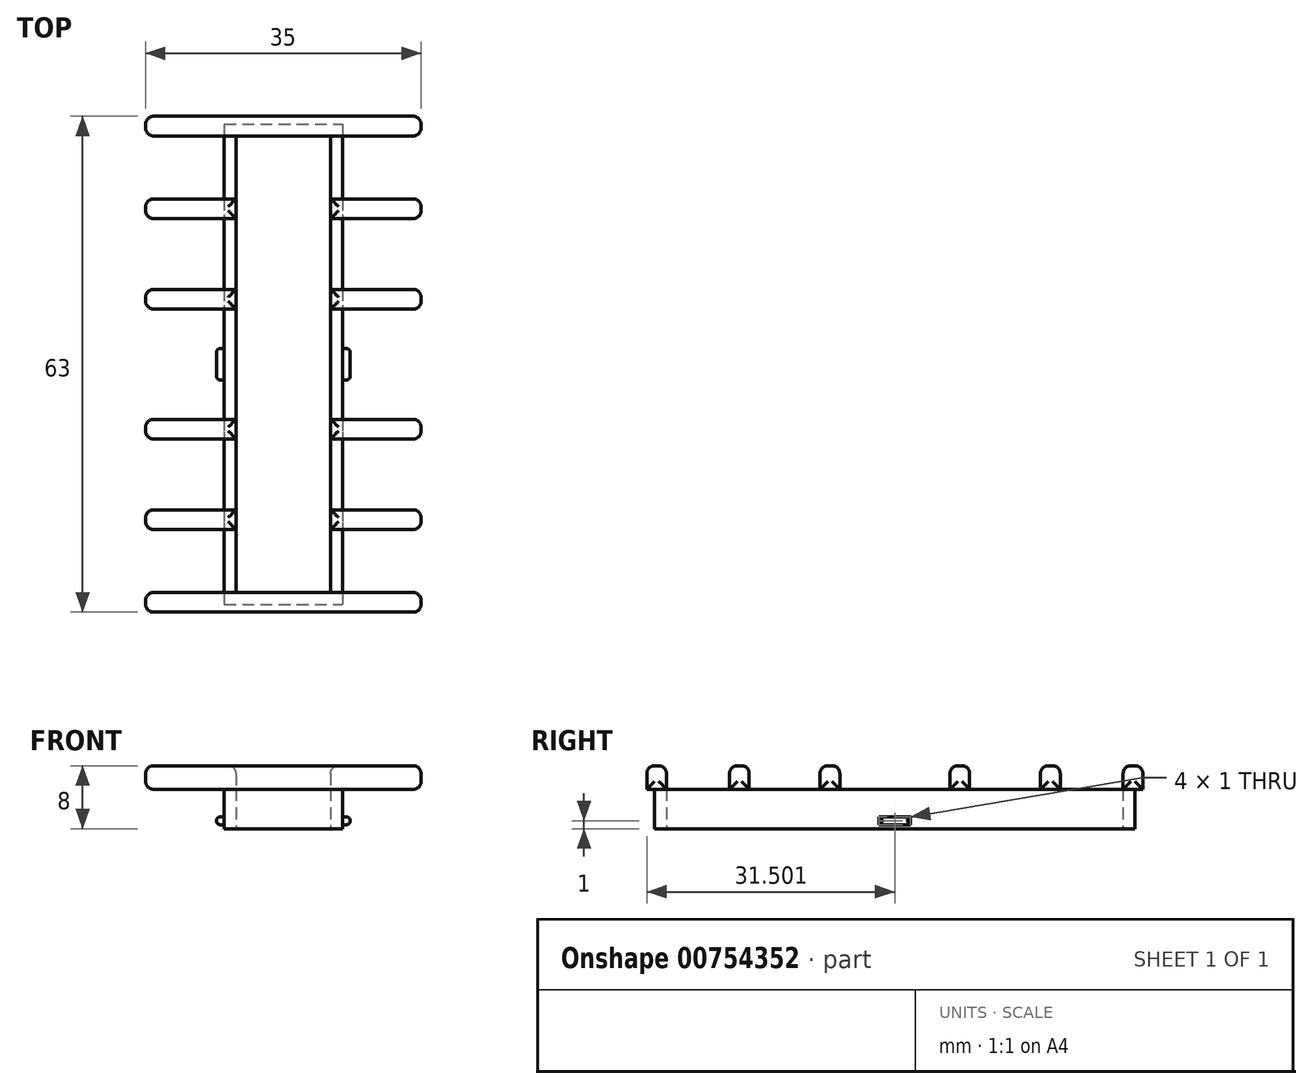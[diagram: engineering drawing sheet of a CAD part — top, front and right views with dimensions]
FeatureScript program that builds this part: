
annotation { "Feature Type Name" : "Feature", "Feature Type Description" : "" }
export const myFeature = defineFeature(function(context is Context, id is Id, definition is map)
    precondition{}
    {
        {
            var Q0;
            Q0=qCreatedBy(makeId("Top.planeOp"),FACE);
            var sketch = newSketch(context, id + "F0", { "sketchPlane" : qUnion([Q0])});
            skLineSegment(sketch, "E0.bottom", {"start": v(-47.35, 57.33) * mm, "end": v(-32.35, 57.33) * mm});
            skLineSegment(sketch, "E0.top", {"start": v(-47.35, -3.67) * mm, "end": v(-32.35, -3.67) * mm});
            skLineSegment(sketch, "E0.left", {"start": v(-47.35, 57.33) * mm, "end": v(-47.35, -3.67) * mm});
            skLineSegment(sketch, "E0.right", {"start": v(-32.35, 57.33) * mm, "end": v(-32.35, -3.67) * mm});
            skLineSegment(sketch, "E1.0", {"start": v(-45.85, 55.83) * mm, "end": v(-33.85, 55.83) * mm});
            skLineSegment(sketch, "E1.1", {"start": v(-45.85, 55.83) * mm, "end": v(-45.85, -2.17) * mm});
            skLineSegment(sketch, "E1.2", {"start": v(-45.85, -2.17) * mm, "end": v(-33.85, -2.17) * mm});
            skLineSegment(sketch, "E1.3", {"start": v(-33.85, 55.83) * mm, "end": v(-33.85, -2.17) * mm});
            skSolve(sketch);
        }
        {
            var Q0;
            Q0 = qSketchRegion(id + "F0", true);
            extrude(context, id + "F1", {"entities" : qUnion([Q0]), "depth" : 5 * mm, "offsetDistance" : 25 * mm});
        }
        {
            var Q0;
            Q0=makeQuery(id+"F1.opExtrude","CAP_FACE",FACE,{"disambiguationData":[OSD([sQuery(id+"F0.wireOp",EDGE,"E0.bottom"),sQuery(id+"F0.wireOp",EDGE,"E0.top"),sQuery(id+"F0.wireOp",EDGE,"E0.left"),sQuery(id+"F0.wireOp",EDGE,"E0.right"),sQuery(id+"F0.wireOp",EDGE,"E1.0"),sQuery(id+"F0.wireOp",EDGE,"E1.1"),sQuery(id+"F0.wireOp",EDGE,"E1.2"),sQuery(id+"F0.wireOp",EDGE,"E1.3")])],"isStart":false});
            var sketch = newSketch(context, id + "F2", { "sketchPlane" : qUnion([Q0])});
            skLineSegment(sketch, "E2.bottom", {"start": v(-39.85, 55.83) * mm, "end": v(-22.35, 55.83) * mm});
            skLineSegment(sketch, "E2.top", {"start": v(-39.85, 58.33) * mm, "end": v(-22.35, 58.33) * mm});
            skLineSegment(sketch, "E2.left", {"start": v(-39.85, 55.83) * mm, "end": v(-39.85, 58.33) * mm});
            skLineSegment(sketch, "E2.right", {"start": v(-22.35, 55.83) * mm, "end": v(-22.35, 58.33) * mm});
            skLineSegment(sketch, "E3.MirrorCS", {"start": v(-39.85, 58.33) * mm, "end": v(-57.35, 58.33) * mm});
            skLineSegment(sketch, "E4.MirrorCS", {"start": v(-39.85, 55.83) * mm, "end": v(-57.35, 55.83) * mm});
            skLineSegment(sketch, "E5.MirrorCS", {"start": v(-57.35, 55.83) * mm, "end": v(-57.35, 58.33) * mm});
            skLineSegment(sketch, "E6.bottom", {"start": v(-39.85, -2.17) * mm, "end": v(-22.35, -2.17) * mm});
            skLineSegment(sketch, "E6.top", {"start": v(-39.85, -4.67) * mm, "end": v(-22.35, -4.67) * mm});
            skLineSegment(sketch, "E6.left", {"start": v(-39.85, -2.17) * mm, "end": v(-39.85, -4.67) * mm});
            skLineSegment(sketch, "E6.right", {"start": v(-22.35, -2.17) * mm, "end": v(-22.35, -4.67) * mm});
            skLineSegment(sketch, "E7.MirrorCS", {"start": v(-39.85, -2.17) * mm, "end": v(-57.35, -2.17) * mm});
            skLineSegment(sketch, "E8.MirrorCS", {"start": v(-57.35, -2.17) * mm, "end": v(-57.35, -4.67) * mm});
            skLineSegment(sketch, "E9.MirrorCS", {"start": v(-39.85, -4.67) * mm, "end": v(-57.35, -4.67) * mm});
            skLineSegment(sketch, "E10.bottom", {"start": v(-33.85, 36.33) * mm, "end": v(-22.35, 36.33) * mm});
            skLineSegment(sketch, "E10.top", {"start": v(-33.85, 33.83) * mm, "end": v(-22.35, 33.83) * mm});
            skLineSegment(sketch, "E10.left", {"start": v(-33.85, 36.33) * mm, "end": v(-33.85, 33.83) * mm});
            skLineSegment(sketch, "E10.right", {"start": v(-22.35, 36.33) * mm, "end": v(-22.35, 33.83) * mm});
            skLineSegment(sketch, "E11.bottom", {"start": v(-33.85, 19.83) * mm, "end": v(-22.35, 19.83) * mm});
            skLineSegment(sketch, "E11.top", {"start": v(-33.85, 17.33) * mm, "end": v(-22.35, 17.33) * mm});
            skLineSegment(sketch, "E11.left", {"start": v(-33.85, 19.83) * mm, "end": v(-33.85, 17.33) * mm});
            skLineSegment(sketch, "E11.right", {"start": v(-22.35, 19.83) * mm, "end": v(-22.35, 17.33) * mm});
            skLineSegment(sketch, "E12.bottom", {"start": v(-45.85, 17.33) * mm, "end": v(-57.35, 17.33) * mm});
            skLineSegment(sketch, "E12.top", {"start": v(-45.85, 19.83) * mm, "end": v(-57.35, 19.83) * mm});
            skLineSegment(sketch, "E12.left", {"start": v(-45.85, 17.33) * mm, "end": v(-45.85, 19.83) * mm});
            skLineSegment(sketch, "E12.right", {"start": v(-57.35, 17.33) * mm, "end": v(-57.35, 19.83) * mm});
            skLineSegment(sketch, "E13.bottom", {"start": v(-45.85, 33.83) * mm, "end": v(-57.35, 33.83) * mm});
            skLineSegment(sketch, "E13.top", {"start": v(-45.85, 36.33) * mm, "end": v(-57.35, 36.33) * mm});
            skLineSegment(sketch, "E13.left", {"start": v(-45.85, 33.83) * mm, "end": v(-45.85, 36.33) * mm});
            skLineSegment(sketch, "E13.right", {"start": v(-57.35, 33.83) * mm, "end": v(-57.35, 36.33) * mm});
            skLineSegment(sketch, "E14.bottom", {"start": v(-33.85, 47.83) * mm, "end": v(-22.35, 47.83) * mm});
            skLineSegment(sketch, "E14.top", {"start": v(-33.85, 45.33) * mm, "end": v(-22.35, 45.33) * mm});
            skLineSegment(sketch, "E14.left", {"start": v(-33.85, 47.83) * mm, "end": v(-33.85, 45.33) * mm});
            skLineSegment(sketch, "E14.right", {"start": v(-22.35, 47.83) * mm, "end": v(-22.35, 45.33) * mm});
            skLineSegment(sketch, "E15.bottom", {"start": v(-33.85, 8.33) * mm, "end": v(-22.35, 8.33) * mm});
            skLineSegment(sketch, "E15.top", {"start": v(-33.85, 5.83) * mm, "end": v(-22.35, 5.83) * mm});
            skLineSegment(sketch, "E15.left", {"start": v(-33.85, 8.33) * mm, "end": v(-33.85, 5.83) * mm});
            skLineSegment(sketch, "E15.right", {"start": v(-22.35, 8.33) * mm, "end": v(-22.35, 5.83) * mm});
            skLineSegment(sketch, "E16.bottom", {"start": v(-45.85, 45.33) * mm, "end": v(-57.35, 45.33) * mm});
            skLineSegment(sketch, "E16.top", {"start": v(-45.85, 47.83) * mm, "end": v(-57.35, 47.83) * mm});
            skLineSegment(sketch, "E16.left", {"start": v(-45.85, 45.33) * mm, "end": v(-45.85, 47.83) * mm});
            skLineSegment(sketch, "E16.right", {"start": v(-57.35, 45.33) * mm, "end": v(-57.35, 47.83) * mm});
            skLineSegment(sketch, "E17.bottom", {"start": v(-45.85, 5.83) * mm, "end": v(-57.35, 5.83) * mm});
            skLineSegment(sketch, "E17.top", {"start": v(-45.85, 8.33) * mm, "end": v(-57.35, 8.33) * mm});
            skLineSegment(sketch, "E17.left", {"start": v(-45.85, 5.83) * mm, "end": v(-45.85, 8.33) * mm});
            skLineSegment(sketch, "E17.right", {"start": v(-57.35, 5.83) * mm, "end": v(-57.35, 8.33) * mm});
            skSolve(sketch);
        }
        {
            var Q0;
            Q0 = qSketchRegion(id + "F2", true);
            extrude(context, id + "F3", {"entities" : qUnion([Q0]), "operationType" : NewBodyOperationType.ADD, "depth" : 3 * mm, "offsetDistance" : 25 * mm});
        }
        {
            var Q0;
            Q0=makeQuery(id+"F3.opExtrude","SWEPT_FACE",FACE,{"disambiguationData":[OSD([sQuery(id+"F2.wireOp",EDGE,"E2.right")])]});
            var Q1;
            Q1=makeQuery(id+"F3.opExtrude","SWEPT_FACE",FACE,{"disambiguationData":[OSD([sQuery(id+"F2.wireOp",EDGE,"E14.right")])]});
            var Q2;
            Q2=makeQuery(id+"F3.opExtrude","SWEPT_FACE",FACE,{"disambiguationData":[OSD([sQuery(id+"F2.wireOp",EDGE,"E10.right")])]});
            var Q3;
            Q3=makeQuery(id+"F3.opExtrude","SWEPT_FACE",FACE,{"disambiguationData":[OSD([sQuery(id+"F2.wireOp",EDGE,"E11.right")])]});
            var Q4;
            Q4=makeQuery(id+"F3.opExtrude","SWEPT_FACE",FACE,{"disambiguationData":[OSD([sQuery(id+"F2.wireOp",EDGE,"E15.right")])]});
            var Q5;
            Q5=makeQuery(id+"F3.opExtrude","SWEPT_FACE",FACE,{"disambiguationData":[OSD([sQuery(id+"F2.wireOp",EDGE,"E6.right")])]});
            var Q6;
            Q6=makeQuery(id+"F3.opExtrude","CAP_EDGE",EDGE,{"disambiguationData":[OSD([sQuery(id+"F2.wireOp",EDGE,"E16.left")])],"isStart":false});
            var Q7;
            Q7=makeQuery(id+"F3.opExtrude","CAP_EDGE",EDGE,{"disambiguationData":[OSD([sQuery(id+"F2.wireOp",EDGE,"E13.left")])],"isStart":false});
            var Q8;
            Q8=makeQuery(id+"F3.opExtrude","CAP_EDGE",EDGE,{"disambiguationData":[OSD([sQuery(id+"F2.wireOp",EDGE,"E12.left")])],"isStart":false});
            var Q9;
            Q9=makeQuery(id+"F3.opExtrude","CAP_EDGE",EDGE,{"disambiguationData":[OSD([sQuery(id+"F2.wireOp",EDGE,"E17.left")])],"isStart":false});
            var Q10;
            Q10=makeQuery(id+"F3.opExtrude","SWEPT_FACE",FACE,{"disambiguationData":[OSD([sQuery(id+"F2.wireOp",EDGE,"E8.MirrorCS")])]});
            var Q11;
            Q11=makeQuery(id+"F3.opExtrude","SWEPT_FACE",FACE,{"disambiguationData":[OSD([sQuery(id+"F2.wireOp",EDGE,"E17.right")])]});
            var Q12;
            Q12=makeQuery(id+"F3.opExtrude","SWEPT_FACE",FACE,{"disambiguationData":[OSD([sQuery(id+"F2.wireOp",EDGE,"E12.right")])]});
            var Q13;
            Q13=makeQuery(id+"F3.opExtrude","SWEPT_FACE",FACE,{"disambiguationData":[OSD([sQuery(id+"F2.wireOp",EDGE,"E13.right")])]});
            var Q14;
            Q14=makeQuery(id+"F3.opExtrude","SWEPT_FACE",FACE,{"disambiguationData":[OSD([sQuery(id+"F2.wireOp",EDGE,"E16.right")])]});
            var Q15;
            Q15=makeQuery(id+"F3.opExtrude","SWEPT_FACE",FACE,{"disambiguationData":[OSD([sQuery(id+"F2.wireOp",EDGE,"E5.MirrorCS")])]});
            var Q16;
            Q16=makeQuery(id+"F3.opExtrude","CAP_EDGE",EDGE,{"disambiguationData":[OSD([sQuery(id+"F2.wireOp",EDGE,"E14.left")])],"isStart":false});
            var Q17;
            Q17=makeQuery(id+"F3.opExtrude","CAP_EDGE",EDGE,{"disambiguationData":[OSD([sQuery(id+"F2.wireOp",EDGE,"E10.left")])],"isStart":false});
            var Q18;
            Q18=makeQuery(id+"F3.opExtrude","CAP_EDGE",EDGE,{"disambiguationData":[OSD([sQuery(id+"F2.wireOp",EDGE,"E11.left")])],"isStart":false});
            var Q19;
            Q19=makeQuery(id+"F3.opExtrude","CAP_EDGE",EDGE,{"disambiguationData":[OSD([sQuery(id+"F2.wireOp",EDGE,"E15.left")])],"isStart":false});
            var Q20;
            Q20=makeQuery(id+"F3.opExtrude","CAP_EDGE",EDGE,{"disambiguationData":[OSD([sQuery(id+"F2.wireOp",EDGE,"E2.bottom"),sQuery(id+"F2.wireOp",EDGE,"E4.MirrorCS")])],"isStart":false});
            var Q21;
            Q21=makeQuery(id+"F3.opExtrude","CAP_EDGE",EDGE,{"disambiguationData":[OSD([sQuery(id+"F2.wireOp",EDGE,"E16.bottom")])],"isStart":false});
            var Q22;
            Q22=makeQuery(id+"F3.opExtrude","CAP_EDGE",EDGE,{"disambiguationData":[OSD([sQuery(id+"F2.wireOp",EDGE,"E14.top")])],"isStart":false});
            var Q23;
            Q23=makeQuery(id+"F3.opExtrude","CAP_EDGE",EDGE,{"disambiguationData":[OSD([sQuery(id+"F2.wireOp",EDGE,"E13.bottom")])],"isStart":false});
            var Q24;
            Q24=makeQuery(id+"F3.opExtrude","CAP_EDGE",EDGE,{"disambiguationData":[OSD([sQuery(id+"F2.wireOp",EDGE,"E10.top")])],"isStart":false});
            var Q25;
            Q25=makeQuery(id+"F3.opExtrude","CAP_EDGE",EDGE,{"disambiguationData":[OSD([sQuery(id+"F2.wireOp",EDGE,"E12.bottom")])],"isStart":false});
            var Q26;
            Q26=makeQuery(id+"F3.opExtrude","CAP_EDGE",EDGE,{"disambiguationData":[OSD([sQuery(id+"F2.wireOp",EDGE,"E11.top")])],"isStart":false});
            var Q27;
            Q27=makeQuery(id+"F3.opExtrude","CAP_EDGE",EDGE,{"disambiguationData":[OSD([sQuery(id+"F2.wireOp",EDGE,"E17.bottom")])],"isStart":false});
            var Q28;
            Q28=makeQuery(id+"F3.opExtrude","CAP_EDGE",EDGE,{"disambiguationData":[OSD([sQuery(id+"F2.wireOp",EDGE,"E15.top")])],"isStart":false});
            var Q29;
            Q29=makeQuery(id+"F3.opExtrude","CAP_EDGE",EDGE,{"disambiguationData":[OSD([sQuery(id+"F2.wireOp",EDGE,"E6.top"),sQuery(id+"F2.wireOp",EDGE,"E9.MirrorCS")])],"isStart":false});
            var Q30;
            Q30=makeQuery(id+"F3.opExtrude","CAP_EDGE",EDGE,{"disambiguationData":[OSD([sQuery(id+"F2.wireOp",EDGE,"E6.bottom"),sQuery(id+"F2.wireOp",EDGE,"E7.MirrorCS")])],"isStart":false});
            var Q31;
            Q31=makeQuery(id+"F3.opExtrude","CAP_EDGE",EDGE,{"disambiguationData":[OSD([sQuery(id+"F2.wireOp",EDGE,"E17.top")])],"isStart":false});
            var Q32;
            Q32=makeQuery(id+"F3.opExtrude","CAP_EDGE",EDGE,{"disambiguationData":[OSD([sQuery(id+"F2.wireOp",EDGE,"E15.bottom")])],"isStart":false});
            var Q33;
            Q33=makeQuery(id+"F3.opExtrude","CAP_EDGE",EDGE,{"disambiguationData":[OSD([sQuery(id+"F2.wireOp",EDGE,"E11.bottom")])],"isStart":false});
            var Q34;
            Q34=makeQuery(id+"F3.opExtrude","CAP_EDGE",EDGE,{"disambiguationData":[OSD([sQuery(id+"F2.wireOp",EDGE,"E12.top")])],"isStart":false});
            var Q35;
            Q35=makeQuery(id+"F3.opExtrude","CAP_EDGE",EDGE,{"disambiguationData":[OSD([sQuery(id+"F2.wireOp",EDGE,"E13.top")])],"isStart":false});
            var Q36;
            Q36=makeQuery(id+"F3.opExtrude","CAP_EDGE",EDGE,{"disambiguationData":[OSD([sQuery(id+"F2.wireOp",EDGE,"E10.bottom")])],"isStart":false});
            var Q37;
            Q37=makeQuery(id+"F3.opExtrude","CAP_EDGE",EDGE,{"disambiguationData":[OSD([sQuery(id+"F2.wireOp",EDGE,"E16.top")])],"isStart":false});
            var Q38;
            Q38=makeQuery(id+"F3.opExtrude","CAP_EDGE",EDGE,{"disambiguationData":[OSD([sQuery(id+"F2.wireOp",EDGE,"E14.bottom")])],"isStart":false});
            var Q39;
            Q39=makeQuery(id+"F3.opExtrude","CAP_EDGE",EDGE,{"disambiguationData":[OSD([sQuery(id+"F2.wireOp",EDGE,"E2.top"),sQuery(id+"F2.wireOp",EDGE,"E3.MirrorCS")])],"isStart":false});
            fillet(context, id + "F4", {"entities" : qUnion([Q0, Q1, Q2, Q3, Q4, Q5, Q6, Q7, Q8, Q9, Q10, Q11, Q12, Q13, Q14, Q15, Q16, Q17, Q18, Q19, Q20, Q21, Q22, Q23, Q24, Q25, Q26, Q27, Q28, Q29, Q30, Q31, Q32, Q33, Q34, Q35, Q36, Q37, Q38, Q39]), "radius" : 1 * mm, "tangentPropagation" : true, "allowEdgeOverflow" : false});
        }
        {
            var Q0;
            Q0=makeQuery(id+"F1.opExtrude","SWEPT_FACE",FACE,{"disambiguationData":[OSD([sQuery(id+"F0.wireOp",EDGE,"E0.right")])]});
            var sketch = newSketch(context, id + "F5", { "sketchPlane" : qUnion([Q0])});
            skLineSegment(sketch, "E18.bottom", {"start": v(28.83, 0.5) * mm, "end": v(24.83, 0.5) * mm});
            skLineSegment(sketch, "E18.top", {"start": v(28.83, 1.5) * mm, "end": v(24.83, 1.5) * mm});
            skLineSegment(sketch, "E18.left", {"start": v(28.83, 0.5) * mm, "end": v(28.83, 1.5) * mm});
            skLineSegment(sketch, "E18.right", {"start": v(24.83, 0.5) * mm, "end": v(24.83, 1.5) * mm});
            skPoint(sketch, "E19.orphan", {"position": v(26.83, 0.5) * mm});
            skSolve(sketch);
        }
        {
            var Q0;
            Q0 = qSketchRegion(id + "F5", true);
            extrude(context, id + "F6", {"entities" : qUnion([Q0]), "operationType" : NewBodyOperationType.ADD, "depth" : 1 * mm, "offsetDistance" : 25 * mm});
        }
        {
            var Q0;
            Q0=makeQuery(id+"F6.opExtrude","CAP_FACE",FACE,{"disambiguationData":[OSD([sQuery(id+"F5.wireOp",EDGE,"E18.bottom"),sQuery(id+"F5.wireOp",EDGE,"E18.top"),sQuery(id+"F5.wireOp",EDGE,"E18.left"),sQuery(id+"F5.wireOp",EDGE,"E18.right")])],"isStart":false});
            fillet(context, id + "F7", {"entities" : qUnion([Q0]), "radius" : 0.5 * mm, "tangentPropagation" : true, "allowEdgeOverflow" : false});
        }
        {
            var Q0;
            Q0=makeQuery(id+"F1.opExtrude","SWEPT_FACE",FACE,{"disambiguationData":[OSD([sQuery(id+"F0.wireOp",EDGE,"E0.left")])]});
            var sketch = newSketch(context, id + "F8", { "sketchPlane" : qUnion([Q0])});
            skLineSegment(sketch, "E20.bottom", {"start": v(-24.83, 0.5) * mm, "end": v(-28.83, 0.5) * mm});
            skLineSegment(sketch, "E20.top", {"start": v(-24.83, 1.5) * mm, "end": v(-28.83, 1.5) * mm});
            skLineSegment(sketch, "E20.left", {"start": v(-24.83, 0.5) * mm, "end": v(-24.83, 1.5) * mm});
            skLineSegment(sketch, "E20.right", {"start": v(-28.83, 0.5) * mm, "end": v(-28.83, 1.5) * mm});
            skPoint(sketch, "E21.endSnap0", {"position": v(-26.83, 0.5) * mm});
            skPoint(sketch, "E21.end.orphan", {"position": v(-26.83, 2.68) * mm});
            skSolve(sketch);
        }
        {
            var Q0;
            Q0 = qSketchRegion(id + "F8", true);
            extrude(context, id + "F9", {"entities" : qUnion([Q0]), "operationType" : NewBodyOperationType.ADD, "depth" : 1 * mm, "offsetDistance" : 25 * mm});
        }
        {
            var Q0;
            Q0=makeQuery(id+"F9.opExtrude","CAP_FACE",FACE,{"disambiguationData":[OSD([sQuery(id+"F8.wireOp",EDGE,"E20.bottom"),sQuery(id+"F8.wireOp",EDGE,"E20.top"),sQuery(id+"F8.wireOp",EDGE,"E20.left"),sQuery(id+"F8.wireOp",EDGE,"E20.right")])],"isStart":false});
            fillet(context, id + "F10", {"entities" : qUnion([Q0]), "radius" : 0.5 * mm, "tangentPropagation" : true, "allowEdgeOverflow" : false});
        }
    });
